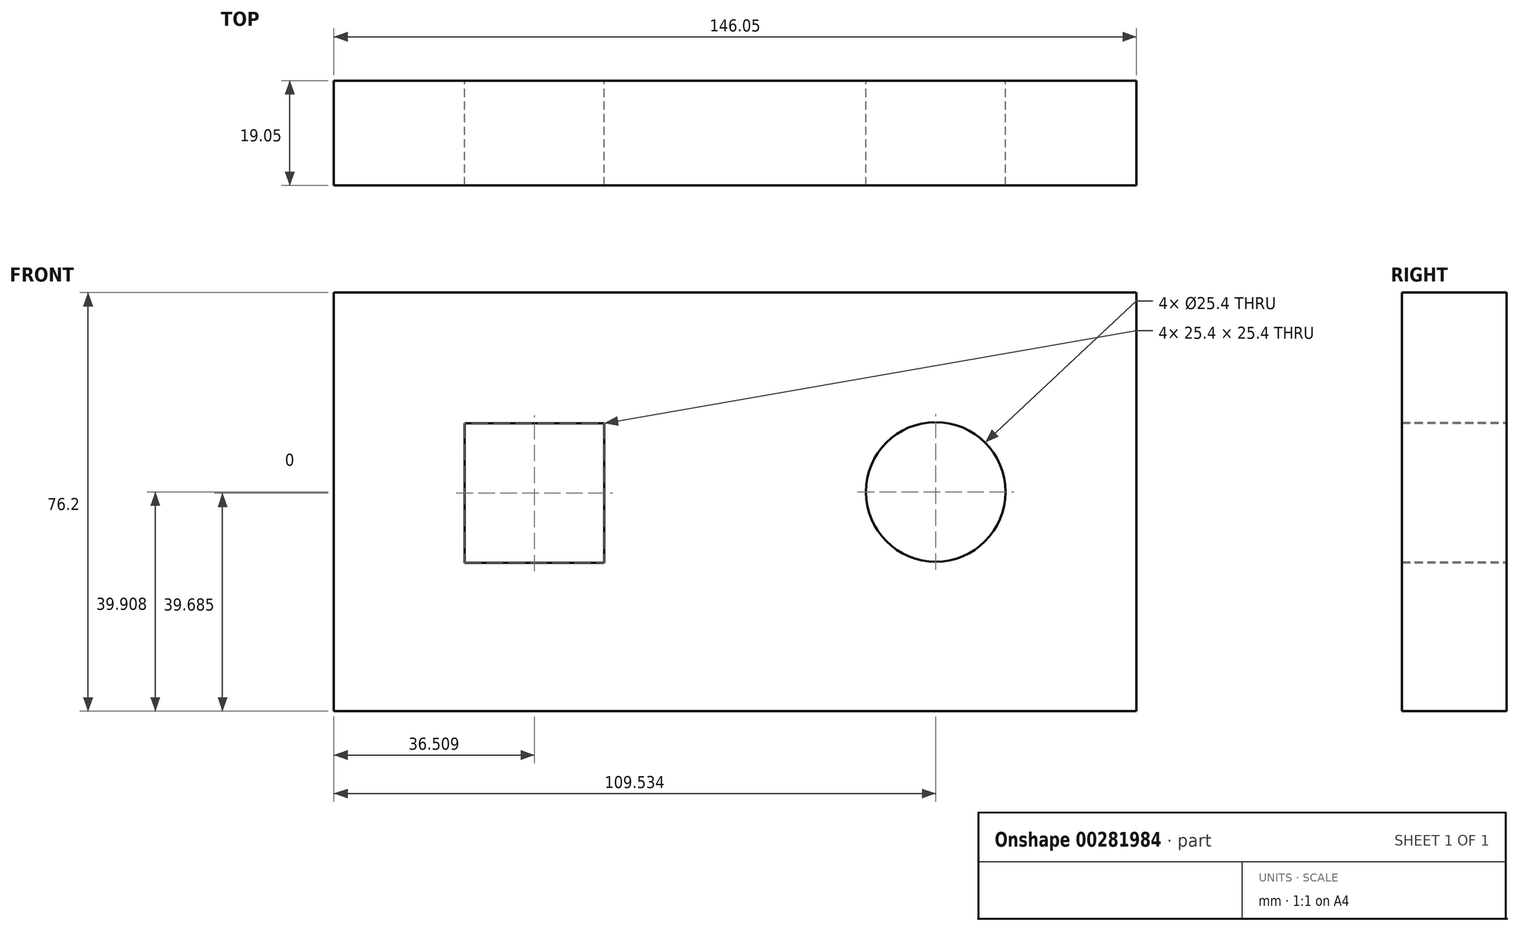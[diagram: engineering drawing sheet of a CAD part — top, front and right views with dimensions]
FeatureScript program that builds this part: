
annotation { "Feature Type Name" : "Feature", "Feature Type Description" : "" }
export const myFeature = defineFeature(function(context is Context, id is Id, definition is map)
    precondition{}
    {
        {
            var Q0;
            Q0=qCreatedBy(makeId("Front.planeOp"),FACE);
            var sketch = newSketch(context, id + "F0", { "sketchPlane" : qUnion([Q0])});
            skLineSegment(sketch, "E0.bottom", {"start": v(-59.92, 70.65) * mm, "end": v(86.13, 70.65) * mm});
            skLineSegment(sketch, "E0.top", {"start": v(-59.92, -5.55) * mm, "end": v(86.13, -5.55) * mm});
            skLineSegment(sketch, "E0.left", {"start": v(-59.92, 70.65) * mm, "end": v(-59.92, -5.55) * mm});
            skLineSegment(sketch, "E0.right", {"start": v(86.13, 70.65) * mm, "end": v(86.13, -5.55) * mm});
            skLineSegment(sketch, "E1", {"start": v(13.1, 70.65) * mm, "end": v(13.1, -5.55) * mm});
            skCircle(sketch, "E2", {"center": v(49.61, 34.36) * mm, "radius": 12.7 * mm});
            skLineSegment(sketch, "E3.bottom", {"start": v(-36.11, 46.84) * mm, "end": v(-10.71, 46.84) * mm});
            skLineSegment(sketch, "E3.top", {"start": v(-36.11, 21.44) * mm, "end": v(-10.71, 21.44) * mm});
            skLineSegment(sketch, "E3.left", {"start": v(-36.11, 46.84) * mm, "end": v(-36.11, 21.44) * mm});
            skLineSegment(sketch, "E3.right", {"start": v(-10.71, 46.84) * mm, "end": v(-10.71, 21.44) * mm});
            skSolve(sketch);
        }
        {
            var Q0;
            {var subQ0=sQuery(id+"F0.wireOp",EDGE,"E0.right");Q0=makeQuery(id+"F0.imprint","IMPRINT",FACE,{"disambiguationData":[TD([[makeQuery(id+"F0.imprint","IMPRINT",EDGE,{"derivedFrom":subQ0}),-1.0]])]});}
            var Q1;
            {var subQ1=sQuery(id+"F0.wireOp",EDGE,"E0.left");Q1=makeQuery(id+"F0.imprint","IMPRINT",FACE,{"disambiguationData":[TD([[makeQuery(id+"F0.imprint","IMPRINT",EDGE,{"derivedFrom":subQ1}),1.0]])]});}
            extrude(context, id + "F1", {"entities" : qUnion([Q0, Q1]), "depth" : 19.05 * mm});
        }
    });
